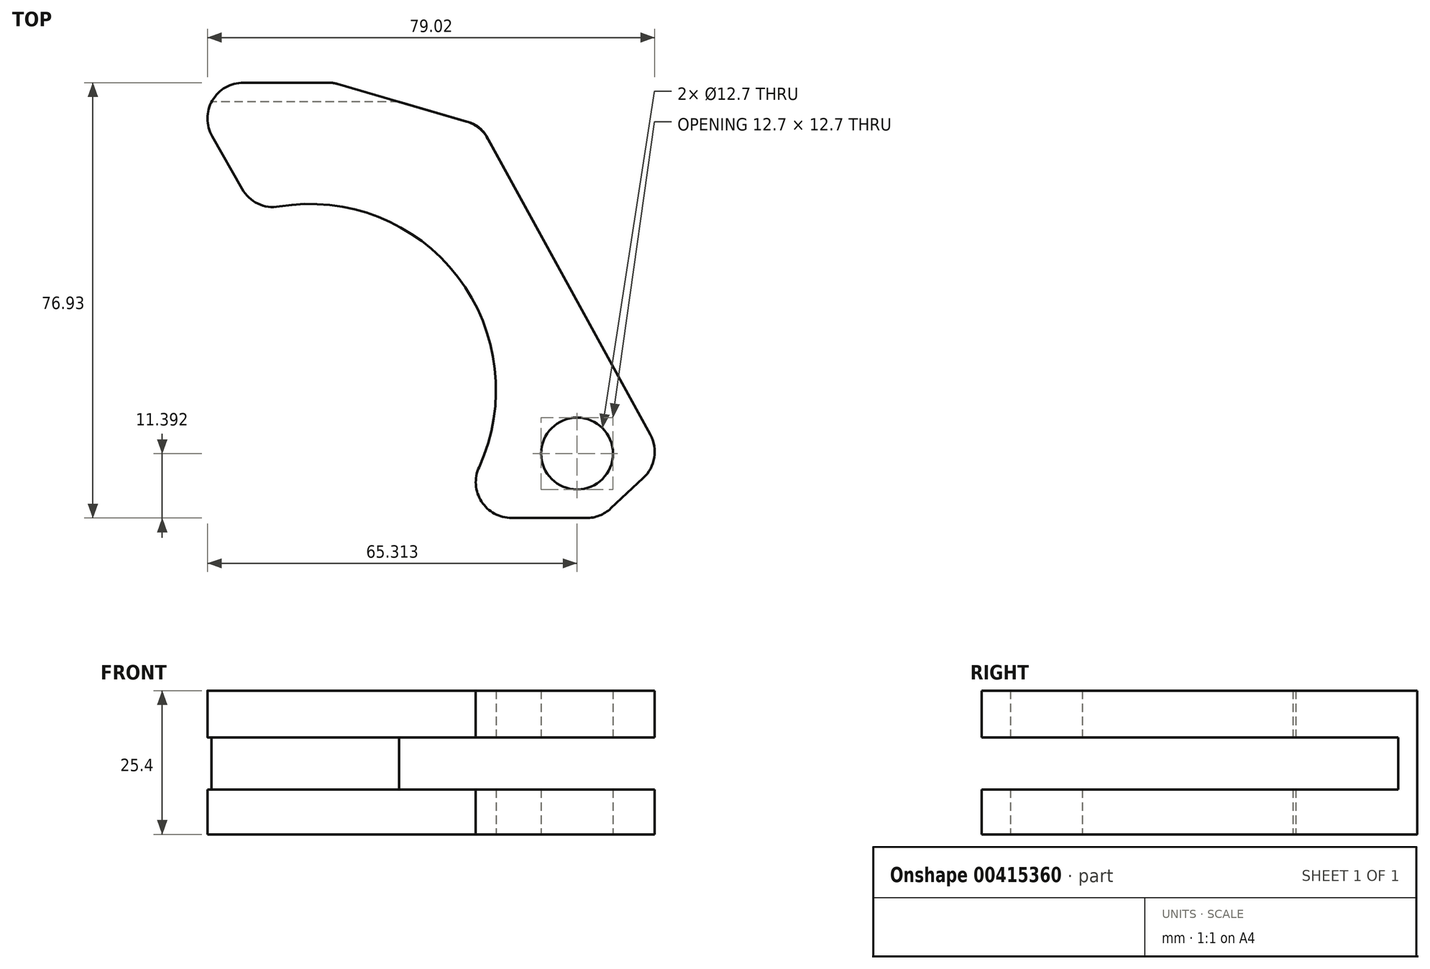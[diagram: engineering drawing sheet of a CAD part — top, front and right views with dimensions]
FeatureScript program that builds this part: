
annotation { "Feature Type Name" : "Feature", "Feature Type Description" : "" }
export const myFeature = defineFeature(function(context is Context, id is Id, definition is map)
    precondition{}
    {
        {
            var Q0;
            Q0=qCreatedBy(makeId("Top.planeOp"),FACE);
            var sketch = newSketch(context, id + "F0", { "sketchPlane" : qUnion([Q0])});
            skLineSegment(sketch, "E0", {"start": v(-25.44, 24.94) * mm, "end": v(-38.46, 47.84) * mm});
            skLineSegment(sketch, "E1", {"start": v(-38.46, 47.84) * mm, "end": v(-11.66, 47.84) * mm});
            skLineSegment(sketch, "E2", {"start": v(-11.66, 47.84) * mm, "end": v(14.38, 40.24) * mm});
            skLineSegment(sketch, "E3", {"start": v(14.38, 40.24) * mm, "end": v(46.71, -18.67) * mm});
            skLineSegment(sketch, "E4", {"start": v(46.71, -18.67) * mm, "end": v(35.54, -29.1) * mm});
            skLineSegment(sketch, "E5", {"start": v(35.54, -29.1) * mm, "end": v(7.98, -29.1) * mm});
            skArc(sketch, "E6", {"start": v(7.98, -29.1) * mm, "mid": v(12.17, 10.86) * mm, "end": v(-25.44, 24.94) * mm});
            skCircle(sketch, "E7", {"center": v(31.41, -17.7) * mm, "radius": 6.35 * mm});
            skSolve(sketch);
        }
        {
            var Q0;
            Q0=qSketchRegion(id+"F0",true);
            extrude(context, id + "F1", {"entities" : qUnion([Q0]), "depth" : 25.4 * mm});
        }
        {
            var Q0;
            Q0=qCreatedBy(makeId("Front.planeOp"),FACE);
            var sketch = newSketch(context, id + "F2", { "sketchPlane" : qUnion([Q0])});
            skLineSegment(sketch, "E8.bottom", {"start": v(67.06, 7.94) * mm, "end": v(-56.26, 7.94) * mm});
            skLineSegment(sketch, "E8.top", {"start": v(67.06, 17.15) * mm, "end": v(-56.26, 17.15) * mm});
            skLineSegment(sketch, "E8.left", {"start": v(67.06, 7.94) * mm, "end": v(67.06, 17.15) * mm});
            skLineSegment(sketch, "E8.right", {"start": v(-56.26, 7.94) * mm, "end": v(-56.26, 17.15) * mm});
            skSolve(sketch);
        }
        {
            var Q0;
            Q0=qSketchRegion(id+"F2",true);
            extrude(context, id + "F3", {"entities" : qUnion([Q0]), "operationType" : NewBodyOperationType.REMOVE, "endBound" : BoundingType.SYMMETRIC, "depth" : 88.9 * mm});
        }
        {
            var Q0;
            {var subQ0=sQuery(id+"F0.wireOp",EDGE,"E3");var subQ1=sQuery(id+"F0.wireOp",EDGE,"E2");Q0=makeQuery(id+"F3.boolean.opBoolean","SPLIT",EDGE,{"disambiguationData":[TD([makeQuery(id+"F3.opExtrude","SWEPT_FACE",FACE,{"disambiguationData":[OSD([sQuery(id+"F2.wireOp",EDGE,"E8.top")])]})])],"derivedFrom":makeQuery(id+"F1.opExtrude","SWEPT_EDGE",EDGE,{"disambiguationData":[OSD([subQ1,subQ0])]})});}
            fillet(context, id + "F4", {"entities" : qUnion([Q0]), "radius" : 6.35 * mm, "tangentPropagation" : true, "allowEdgeOverflow" : false});
        }
        {
            var Q0;
            {var subQ0=sQuery(id+"F0.wireOp",EDGE,"E3");var subQ1=sQuery(id+"F0.wireOp",EDGE,"E2");Q0=makeQuery(id+"F3.boolean.opBoolean","SPLIT",EDGE,{"disambiguationData":[TD([makeQuery(id+"F3.opExtrude","SWEPT_FACE",FACE,{"disambiguationData":[OSD([sQuery(id+"F2.wireOp",EDGE,"E8.bottom")])]})])],"derivedFrom":makeQuery(id+"F1.opExtrude","SWEPT_EDGE",EDGE,{"disambiguationData":[OSD([subQ1,subQ0])]})});}
            fillet(context, id + "F5", {"entities" : qUnion([Q0]), "radius" : 5.08 * mm, "tangentPropagation" : true, "allowEdgeOverflow" : false});
        }
        {
            var Q0;
            Q0=makeQuery(id+"F1.opExtrude","SWEPT_EDGE",EDGE,{"disambiguationData":[OSD([sQuery(id+"F0.wireOp",EDGE,"E1"),sQuery(id+"F0.wireOp",EDGE,"E2")])]});
            fillet(context, id + "F6", {"entities" : qUnion([Q0]), "radius" : 5.08 * mm, "tangentPropagation" : true, "allowEdgeOverflow" : false});
        }
        {
            var Q0;
            {var subQ0=sQuery(id+"F0.wireOp",EDGE,"E6");var subQ1=sQuery(id+"F0.wireOp",EDGE,"E5");Q0=makeQuery(id+"F3.boolean.opBoolean","SPLIT",EDGE,{"disambiguationData":[TD([makeQuery(id+"F3.opExtrude","SWEPT_FACE",FACE,{"disambiguationData":[OSD([sQuery(id+"F2.wireOp",EDGE,"E8.top")])]})])],"derivedFrom":makeQuery(id+"F1.opExtrude","SWEPT_EDGE",EDGE,{"disambiguationData":[OSD([subQ1,subQ0])]})});}
            var Q1;
            {var subQ0=sQuery(id+"F0.wireOp",EDGE,"E6");var subQ1=sQuery(id+"F0.wireOp",EDGE,"E5");Q1=makeQuery(id+"F3.boolean.opBoolean","SPLIT",EDGE,{"disambiguationData":[TD([makeQuery(id+"F3.opExtrude","SWEPT_FACE",FACE,{"disambiguationData":[OSD([sQuery(id+"F2.wireOp",EDGE,"E8.bottom")])]})])],"derivedFrom":makeQuery(id+"F1.opExtrude","SWEPT_EDGE",EDGE,{"disambiguationData":[OSD([subQ1,subQ0])]})});}
            fillet(context, id + "F7", {"entities" : qUnion([Q0, Q1]), "radius" : 6.35 * mm, "tangentPropagation" : true, "allowEdgeOverflow" : false});
        }
        {
            var Q0;
            {var subQ0=sQuery(id+"F0.wireOp",EDGE,"E5");var subQ1=sQuery(id+"F0.wireOp",EDGE,"E4");Q0=makeQuery(id+"F3.boolean.opBoolean","SPLIT",EDGE,{"disambiguationData":[TD([makeQuery(id+"F3.opExtrude","SWEPT_FACE",FACE,{"disambiguationData":[OSD([sQuery(id+"F2.wireOp",EDGE,"E8.bottom")])]})])],"derivedFrom":makeQuery(id+"F1.opExtrude","SWEPT_EDGE",EDGE,{"disambiguationData":[OSD([subQ1,subQ0])]})});}
            var Q1;
            {var subQ0=sQuery(id+"F0.wireOp",EDGE,"E5");var subQ1=sQuery(id+"F0.wireOp",EDGE,"E4");Q1=makeQuery(id+"F3.boolean.opBoolean","SPLIT",EDGE,{"disambiguationData":[TD([makeQuery(id+"F3.opExtrude","SWEPT_FACE",FACE,{"disambiguationData":[OSD([sQuery(id+"F2.wireOp",EDGE,"E8.top")])]})])],"derivedFrom":makeQuery(id+"F1.opExtrude","SWEPT_EDGE",EDGE,{"disambiguationData":[OSD([subQ1,subQ0])]})});}
            var Q2;
            {var subQ0=sQuery(id+"F0.wireOp",EDGE,"E4");var subQ1=sQuery(id+"F0.wireOp",EDGE,"E3");Q2=makeQuery(id+"F3.boolean.opBoolean","SPLIT",EDGE,{"disambiguationData":[TD([makeQuery(id+"F3.opExtrude","SWEPT_FACE",FACE,{"disambiguationData":[OSD([sQuery(id+"F2.wireOp",EDGE,"E8.top")])]})])],"derivedFrom":makeQuery(id+"F1.opExtrude","SWEPT_EDGE",EDGE,{"disambiguationData":[OSD([subQ1,subQ0])]})});}
            var Q3;
            {var subQ0=sQuery(id+"F0.wireOp",EDGE,"E4");var subQ1=sQuery(id+"F0.wireOp",EDGE,"E3");Q3=makeQuery(id+"F3.boolean.opBoolean","SPLIT",EDGE,{"disambiguationData":[TD([makeQuery(id+"F3.opExtrude","SWEPT_FACE",FACE,{"disambiguationData":[OSD([sQuery(id+"F2.wireOp",EDGE,"E8.bottom")])]})])],"derivedFrom":makeQuery(id+"F1.opExtrude","SWEPT_EDGE",EDGE,{"disambiguationData":[OSD([subQ1,subQ0])]})});}
            fillet(context, id + "F8", {"entities" : qUnion([Q0, Q1, Q2, Q3]), "radius" : 6.35 * mm, "tangentPropagation" : true, "allowEdgeOverflow" : false});
        }
        {
            var Q0;
            {var subQ0=sQuery(id+"F0.wireOp",EDGE,"E0");var subQ1=sQuery(id+"F0.wireOp",EDGE,"E6");Q0=makeQuery(id+"F3.boolean.opBoolean","SPLIT",EDGE,{"disambiguationData":[TD([makeQuery(id+"F3.opExtrude","SWEPT_FACE",FACE,{"disambiguationData":[OSD([sQuery(id+"F2.wireOp",EDGE,"E8.bottom")])]})])],"derivedFrom":makeQuery(id+"F1.opExtrude","SWEPT_EDGE",EDGE,{"disambiguationData":[OSD([subQ0,subQ1])]})});}
            var Q1;
            {var subQ0=sQuery(id+"F0.wireOp",EDGE,"E0");var subQ1=sQuery(id+"F0.wireOp",EDGE,"E6");Q1=makeQuery(id+"F3.boolean.opBoolean","SPLIT",EDGE,{"disambiguationData":[TD([makeQuery(id+"F3.opExtrude","SWEPT_FACE",FACE,{"disambiguationData":[OSD([sQuery(id+"F2.wireOp",EDGE,"E8.top")])]})])],"derivedFrom":makeQuery(id+"F1.opExtrude","SWEPT_EDGE",EDGE,{"disambiguationData":[OSD([subQ0,subQ1])]})});}
            var Q2;
            Q2=makeQuery(id+"F1.opExtrude","SWEPT_EDGE",EDGE,{"disambiguationData":[OSD([sQuery(id+"F0.wireOp",EDGE,"E0"),sQuery(id+"F0.wireOp",EDGE,"E1")])]});
            fillet(context, id + "F9", {"entities" : qUnion([Q0, Q1, Q2]), "radius" : 6.35 * mm, "tangentPropagation" : true, "allowEdgeOverflow" : false});
        }
    });
